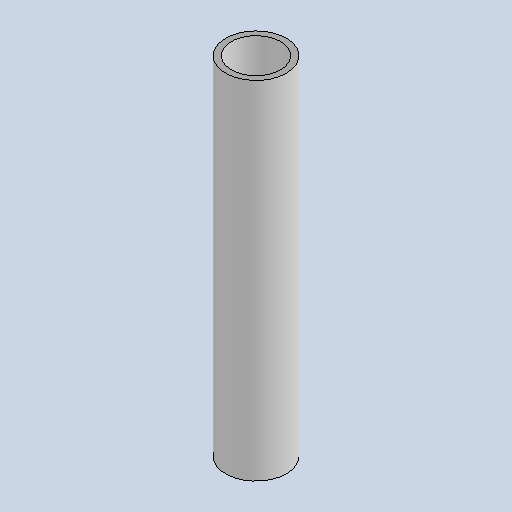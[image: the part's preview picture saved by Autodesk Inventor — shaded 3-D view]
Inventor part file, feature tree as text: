
AUTODESK INVENTOR PART (.ipt)
format: ipt  version: 2025.1 (Build 291241020, 241B)  size: 118,272 bytes
history: native  units: mm
features: extrude x1, sketch x1
ambient origin geometry x8: Origin, YZ Plane, XZ Plane, XY Plane, X Axis, Y Axis, Z Axis, Center Point
bodies: Body1 (feature_tree)
feature tree (2):
  extrude  "Extrusion5"  Depth=120.0mm
  sketch  "Sketch11"  dims[d187=21.0mm d188=2.0mm d189=120.0mm d190=0.0mm]
